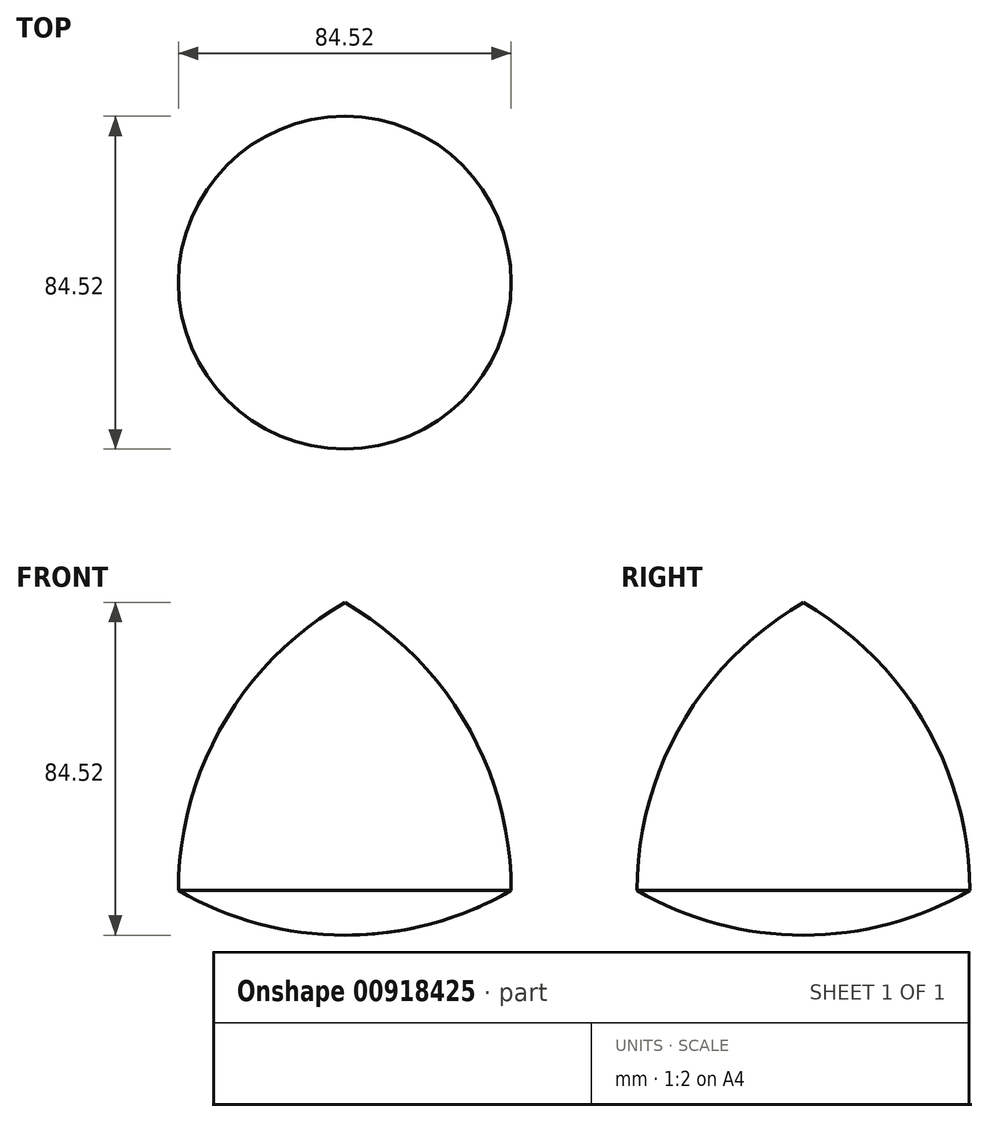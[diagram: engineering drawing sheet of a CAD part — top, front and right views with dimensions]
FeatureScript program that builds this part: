
annotation { "Feature Type Name" : "Feature", "Feature Type Description" : "" }
export const myFeature = defineFeature(function(context is Context, id is Id, definition is map)
    precondition{}
    {
        {
            var Q0;
            Q0=qCreatedBy(makeId("Front.planeOp"),FACE);
            var sketch = newSketch(context, id + "F0", { "sketchPlane" : qUnion([Q0])});
            skLineSegment(sketch, "E0", {"start": v(0, 73.2) * mm, "end": v(-42.26, 0) * mm, "construction": true});
            skLineSegment(sketch, "E1", {"start": v(-42.26, 0) * mm, "end": v(42.26, 0) * mm, "construction": true});
            skLineSegment(sketch, "E2", {"start": v(42.26, 0) * mm, "end": v(0, 73.2) * mm, "construction": true});
            skArc(sketch, "E3", {"start": v(-42.26, 0) * mm, "mid": v(0, -11.32) * mm, "end": v(42.26, 0) * mm});
            skArc(sketch, "E4", {"start": v(42.26, 0) * mm, "mid": v(30.94, 42.26) * mm, "end": v(0, 73.2) * mm});
            skArc(sketch, "E5", {"start": v(0, 73.2) * mm, "mid": v(-30.94, 42.26) * mm, "end": v(-42.26, 0) * mm});
            skLineSegment(sketch, "E6", {"start": v(0, 73.2) * mm, "end": v(0, -11.32) * mm});
            skSolve(sketch);
        }
        {
            var Q0;
            {var subQ0=sQuery(id+"F0.wireOp",EDGE,"E4");Q0=makeQuery(id+"F0.imprint","IMPRINT",FACE,{"disambiguationData":[TD([[makeQuery(id+"F0.imprint","IMPRINT",EDGE,{"derivedFrom":subQ0}),1.0]])]});}
            var Q1;
            Q1=sQuery(id+"F0.wireOp",EDGE,"E6");
            revolve(context, id + "F1", {"surfaceOperationType" : NewSurfaceOperationType.NEW, "entities" : qUnion([Q0]), "axis" : qUnion([Q1]), "revolveType" : RevolveType.FULL});
        }
    });
